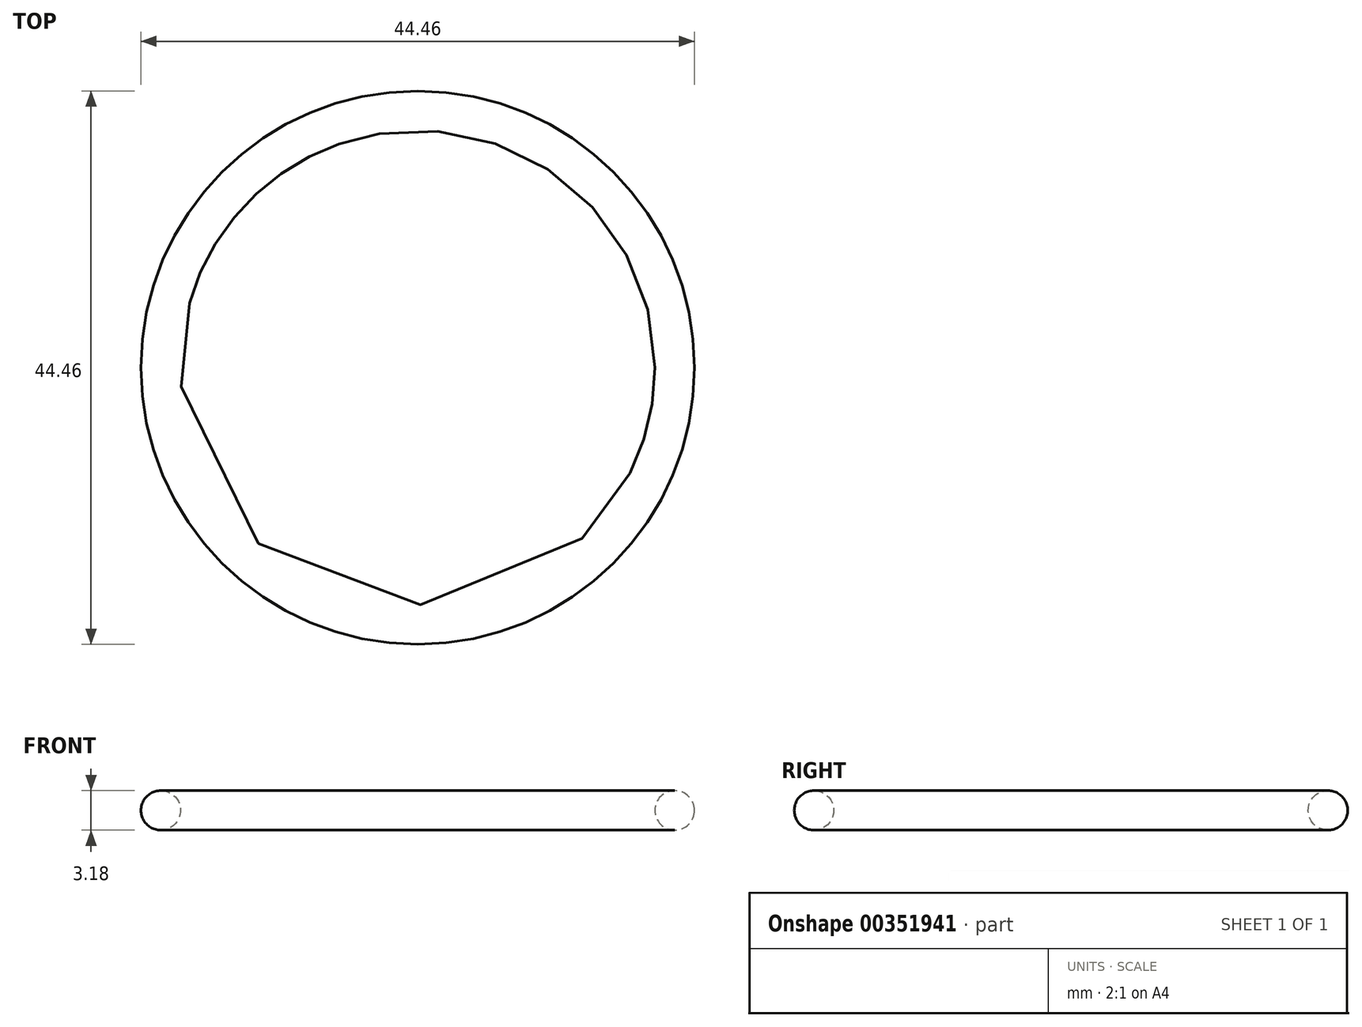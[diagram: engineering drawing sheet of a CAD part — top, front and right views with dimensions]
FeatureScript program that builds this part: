
annotation { "Feature Type Name" : "Feature", "Feature Type Description" : "" }
export const myFeature = defineFeature(function(context is Context, id is Id, definition is map)
    precondition{}
    {
        {
            var Q0;
            Q0=qCreatedBy(makeId("Front.planeOp"),FACE);
            var sketch = newSketch(context, id + "F0", { "sketchPlane" : qUnion([Q0])});
            skCircle(sketch, "E0", {"center": v(-20.64, 0) * mm, "radius": 1.59 * mm});
            skLineSegment(sketch, "E1", {"start": v(0, 15.02) * mm, "end": v(0, -15.02) * mm, "construction": true});
            skSolve(sketch);
        }
        {
            var Q0;
            Q0 = qSketchRegion(id + "F0", true);
            var Q1;
            Q1=sQuery(id+"F0.wireOp",EDGE,"E1");
            revolve(context, id + "F1", {"entities" : qUnion([Q0]), "axis" : qUnion([Q1]), "revolveType" : RevolveType.FULL});
        }
    });
